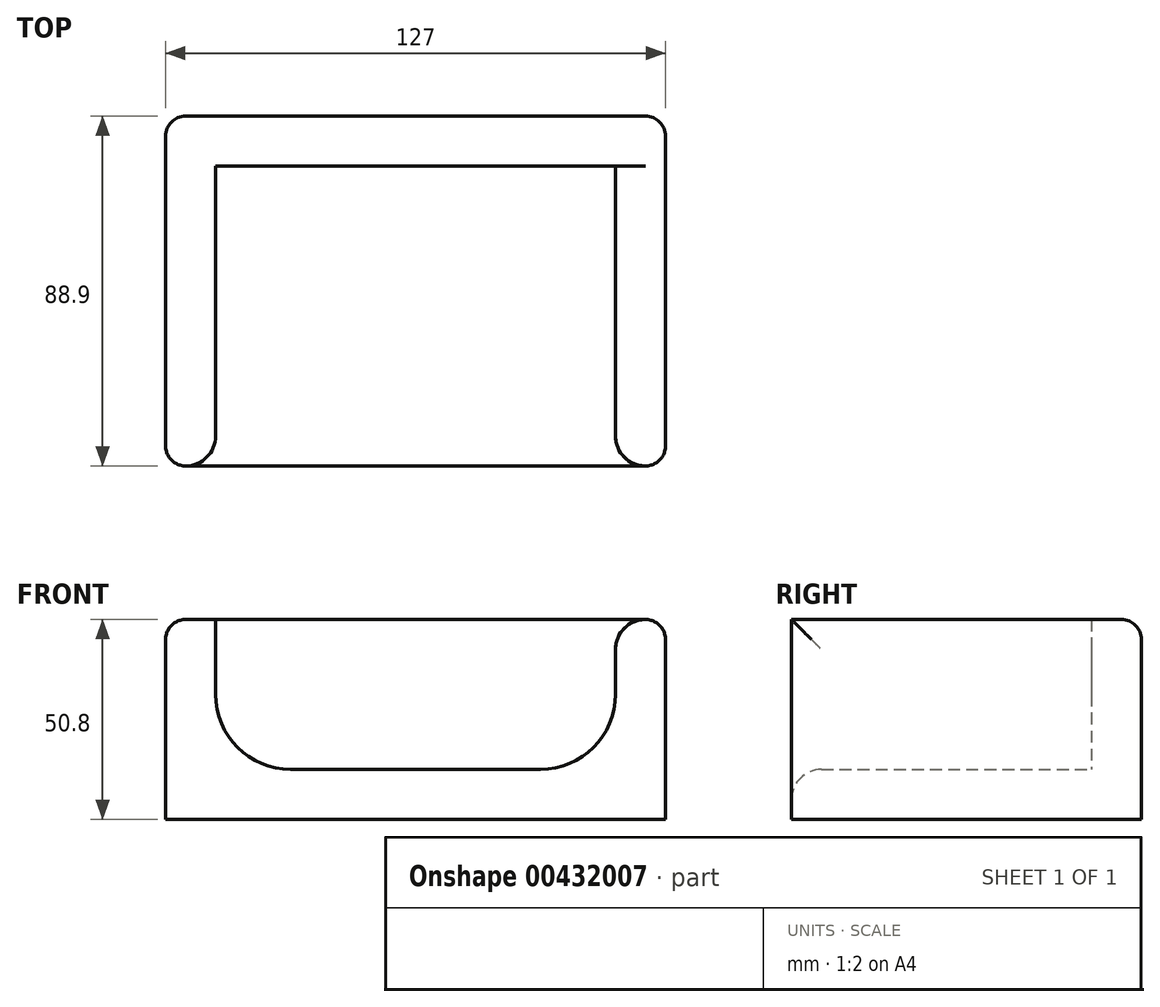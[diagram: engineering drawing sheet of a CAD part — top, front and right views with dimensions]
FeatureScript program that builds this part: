
annotation { "Feature Type Name" : "Feature", "Feature Type Description" : "" }
export const myFeature = defineFeature(function(context is Context, id is Id, definition is map)
    precondition{}
    {
        {
            var Q0;
            Q0=qCreatedBy(makeId("Front.planeOp"),FACE);
            var sketch = newSketch(context, id + "F0", { "sketchPlane" : qUnion([Q0])});
            skLineSegment(sketch, "E0", {"start": v(-63.5, 0) * mm, "end": v(-63.5, 50.8) * mm});
            skLineSegment(sketch, "E1", {"start": v(-63.5, 50.8) * mm, "end": v(-50.8, 50.8) * mm});
            skLineSegment(sketch, "E2", {"start": v(-63.5, 0) * mm, "end": v(0, 0) * mm});
            skLineSegment(sketch, "E3", {"start": v(0, -25.36) * mm, "end": v(0, 47.17) * mm, "construction": true});
            skLineSegment(sketch, "E4.MirrorCS", {"start": v(63.5, 50.8) * mm, "end": v(50.8, 50.8) * mm});
            skLineSegment(sketch, "E5.MirrorCS", {"start": v(63.5, 0) * mm, "end": v(63.5, 50.8) * mm});
            skLineSegment(sketch, "E6.MirrorCS", {"start": v(63.5, 0) * mm, "end": v(0, 0) * mm});
            skLineSegment(sketch, "E7", {"start": v(-50.8, 50.8) * mm, "end": v(-50.8, 12.7) * mm});
            skLineSegment(sketch, "E8", {"start": v(-50.8, 12.7) * mm, "end": v(0, 12.7) * mm});
            skLineSegment(sketch, "E9.MirrorCS", {"start": v(50.8, 12.7) * mm, "end": v(0, 12.7) * mm});
            skLineSegment(sketch, "E10.MirrorCS", {"start": v(50.8, 50.8) * mm, "end": v(50.8, 12.7) * mm});
            skSolve(sketch);
        }
        {
            var Q0;
            Q0 = qSketchRegion(id + "F0", true);
            extrude(context, id + "F1", {"entities" : qUnion([Q0]), "depth" : 76.2 * mm});
        }
        {
            var Q0;
            Q0=qCreatedBy(makeId("Front.planeOp"),FACE);
            var sketch = newSketch(context, id + "F2", { "sketchPlane" : qUnion([Q0])});
            skLineSegment(sketch, "E11.bottom", {"start": v(-63.5, 50.8) * mm, "end": v(63.5, 50.8) * mm});
            skLineSegment(sketch, "E11.top", {"start": v(-63.5, 0) * mm, "end": v(63.5, 0) * mm});
            skLineSegment(sketch, "E11.left", {"start": v(-63.5, 50.8) * mm, "end": v(-63.5, 0) * mm});
            skLineSegment(sketch, "E11.right", {"start": v(63.5, 50.8) * mm, "end": v(63.5, 0) * mm});
            skSolve(sketch);
        }
        {
            var Q0;
            Q0=makeQuery(id+"F2.imprint","IMPRINT",FACE,{"disambiguationData":[TD([[makeQuery(id+"F2.imprint","IMPRINT",EDGE,{"derivedFrom":sQuery(id+"F2.wireOp",EDGE,"E11.bottom")}),-1.0]])]});
            extrude(context, id + "F3", {"entities" : qUnion([Q0]), "operationType" : NewBodyOperationType.ADD, "oppositeDirection" : true, "depth" : 12.7 * mm});
        }
        {
            var Q0;
            Q0=makeQuery(id+"F1.opExtrude","SWEPT_EDGE",EDGE,{"disambiguationData":[OSD([sQuery(id+"F0.wireOp",EDGE,"E9.MirrorCS"),sQuery(id+"F0.wireOp",EDGE,"E10.MirrorCS")])]});
            var Q1;
            Q1=makeQuery(id+"F1.opExtrude","CAP_EDGE",EDGE,{"disambiguationData":[OSD([sQuery(id+"F0.wireOp",EDGE,"E8"),sQuery(id+"F0.wireOp",EDGE,"E9.MirrorCS")])],"isStart":true});
            var Q2;
            Q2=makeQuery(id+"F1.opExtrude","SWEPT_EDGE",EDGE,{"disambiguationData":[OSD([sQuery(id+"F0.wireOp",EDGE,"E7"),sQuery(id+"F0.wireOp",EDGE,"E8")])]});
            fillet(context, id + "F4", {"entities" : qUnion([Q0, Q1, Q2]), "radius" : 19.05 * mm, "tangentPropagation" : true, "allowEdgeOverflow" : false});
        }
        {
            var Q0;
            Q0=makeQuery(id+"F1.opExtrude","CAP_EDGE",EDGE,{"disambiguationData":[OSD([sQuery(id+"F0.wireOp",EDGE,"E7")])],"isStart":true});
            var Q1;
            Q1=makeQuery(id+"F1.opExtrude","CAP_EDGE",EDGE,{"disambiguationData":[OSD([sQuery(id+"F0.wireOp",EDGE,"E10.MirrorCS")])],"isStart":true});
            var Q2;
            Q2=makeQuery(id+"F1.opExtrude","SWEPT_EDGE",EDGE,{"disambiguationData":[OSD([sQuery(id+"F0.wireOp",EDGE,"E4.MirrorCS"),sQuery(id+"F0.wireOp",EDGE,"E10.MirrorCS")])]});
            var Q3;
            Q3=makeQuery(id+"F1.opExtrude","CAP_EDGE",EDGE,{"disambiguationData":[OSD([sQuery(id+"F0.wireOp",EDGE,"E8"),sQuery(id+"F0.wireOp",EDGE,"E9.MirrorCS")])],"isStart":false});
            fillet(context, id + "F5", {"entities" : qUnion([Q0, Q1, Q2, Q3]), "radius" : 7.62 * mm, "tangentPropagation" : true, "allowEdgeOverflow" : false});
        }
        {
            var Q0;
            Q0=makeQuery(id+"F3.boolean.opBoolean","MERGE",EDGE,{"derivedFrom":[makeQuery(id+"F1.opExtrude","SWEPT_EDGE",EDGE,{"disambiguationData":[OSD([sQuery(id+"F0.wireOp",EDGE,"E0"),sQuery(id+"F0.wireOp",EDGE,"E1")])]}),makeQuery(id+"F3.opExtrude","SWEPT_EDGE",EDGE,{"disambiguationData":[OSD([sQuery(id+"F2.wireOp",EDGE,"E11.bottom"),sQuery(id+"F2.wireOp",EDGE,"E11.left")])]})]});
            var Q1;
            Q1=makeQuery(id+"F3.opExtrude","CAP_EDGE",EDGE,{"disambiguationData":[OSD([sQuery(id+"F2.wireOp",EDGE,"E11.bottom")])],"isStart":false});
            var Q2;
            Q2=makeQuery(id+"F3.boolean.opBoolean","MERGE",EDGE,{"derivedFrom":[makeQuery(id+"F1.opExtrude","SWEPT_EDGE",EDGE,{"disambiguationData":[OSD([sQuery(id+"F0.wireOp",EDGE,"E4.MirrorCS"),sQuery(id+"F0.wireOp",EDGE,"E5.MirrorCS")])]}),makeQuery(id+"F3.opExtrude","SWEPT_EDGE",EDGE,{"disambiguationData":[OSD([sQuery(id+"F2.wireOp",EDGE,"E11.bottom"),sQuery(id+"F2.wireOp",EDGE,"E11.right")])]})]});
            var Q3;
            Q3=makeQuery(id+"F1.opExtrude","CAP_EDGE",EDGE,{"disambiguationData":[OSD([sQuery(id+"F0.wireOp",EDGE,"E5.MirrorCS")])],"isStart":false});
            var Q4;
            Q4=makeQuery(id+"F1.opExtrude","CAP_EDGE",EDGE,{"disambiguationData":[OSD([sQuery(id+"F0.wireOp",EDGE,"E0")])],"isStart":false});
            var Q5;
            Q5=makeQuery(id+"F3.opExtrude","CAP_EDGE",EDGE,{"disambiguationData":[OSD([sQuery(id+"F2.wireOp",EDGE,"E11.left")])],"isStart":false});
            var Q6;
            Q6=makeQuery(id+"F3.opExtrude","CAP_EDGE",EDGE,{"disambiguationData":[OSD([sQuery(id+"F2.wireOp",EDGE,"E11.right")])],"isStart":false});
            fillet(context, id + "F6", {"entities" : qUnion([Q0, Q1, Q2, Q3, Q4, Q5, Q6]), "radius" : 5.08 * mm, "tangentPropagation" : true, "allowEdgeOverflow" : false});
        }
    });
